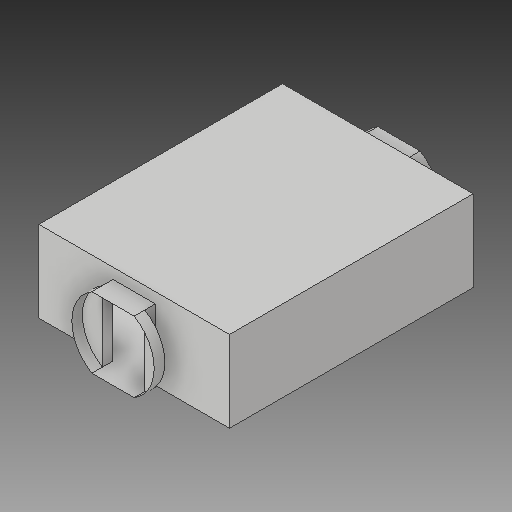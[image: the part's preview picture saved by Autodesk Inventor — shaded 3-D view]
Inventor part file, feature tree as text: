
AUTODESK INVENTOR PART (.ipt)
format: ipt  version: 2017 (Build 210142000, 142)  size: 183,808 bytes
history: native  units: in
note: dims shown in document units (in); Inventor stores cm internally (conversion verified against a paired STEP export)
features: extrude x5, sketch x5, other x1, mirror x1, delete_face x1
ambient origin geometry x8: Origin, YZ Plane, XZ Plane, XY Plane, X Axis, Y Axis, Z Axis, Center Point
bodies: Solid1 (feature_tree)
feature tree (13):
  extrude  "floor"  Depth=25.0in
  extrude  "walls"  Depth=1.0in
  extrude  "doorframe"  Depth=1.0in
  extrude  "ceiling"  Depth=1.0in TaperAngle=0.0deg
  sketch  "Sketch10"  dims[d17=2.0in d18=6.6667in d20=8.6667in d21=0.0in d22=1.0in d23=0.0in d37=6.6667in d40=1.0in d41=0.0in d58=4.0in d60=3.8873in d61=3.8873in d65=1.6458in d71=3.3333in d73=1.0in d76=1.0in]
  extrude  "corridor connect"  Depth=6.6667in
  other  "middle of the room"
  mirror  "Mirror connection for starting door"
  delete_face  "Delete Face1"
  sketch  "Sketch1"  dims[d0=20.0in d1=25.0in]
  sketch  "Sketch4"  dims[d2=1.0in d3=0.0in d11=1.0in]
  sketch  "Sketch5"  dims[d12=1.0in d13=1.0in]
  sketch  "Sketch7"  dims[d14=1.0in d15=8.6667in d16=0.0in]
